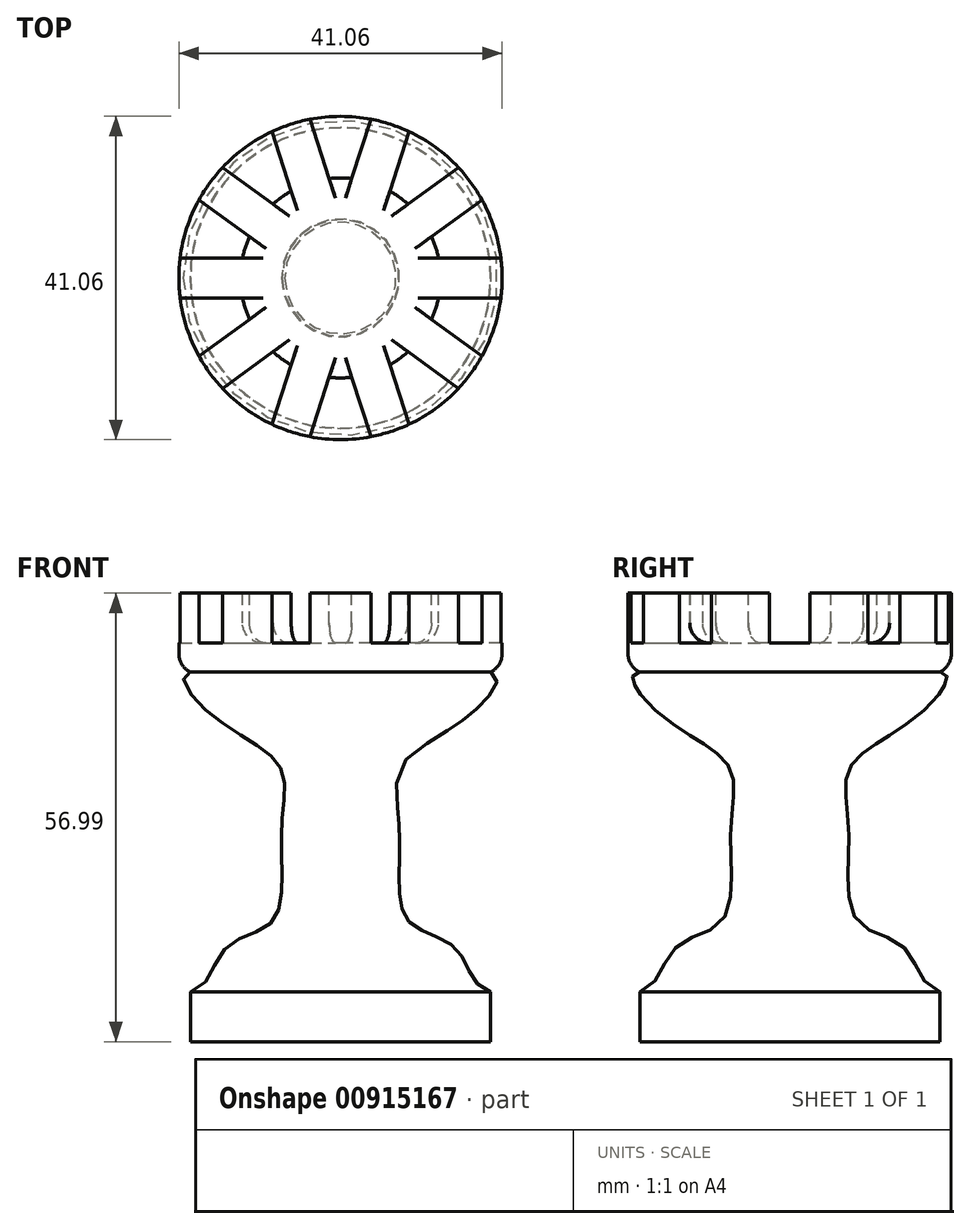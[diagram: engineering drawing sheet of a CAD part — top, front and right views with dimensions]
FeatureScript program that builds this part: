
annotation { "Feature Type Name" : "Feature", "Feature Type Description" : "" }
export const myFeature = defineFeature(function(context is Context, id is Id, definition is map)
    precondition{}
    {
        {
            var Q0;
            Q0=qCreatedBy(makeId("Front.planeOp"),FACE);
            var sketch = newSketch(context, id + "F0", { "sketchPlane" : qUnion([Q0])});
            skLineSegment(sketch, "E0", {"start": v(0, 0) * mm, "end": v(0, 57.15) * mm});
            skLineSegment(sketch, "E1", {"start": v(0, 0) * mm, "end": v(19.05, 0) * mm});
            skLineSegment(sketch, "E2", {"start": v(19.05, 0) * mm, "end": v(19.05, 6.35) * mm});
            skLineSegment(sketch, "E3", {"start": v(0, 47) * mm, "end": v(32.66, 47) * mm, "construction": true});
            skFitSpline(sketch, "E4", {"points": [v(19.05, 6.35) * mm, v(14.72, 11.76) * mm, v(8.88, 15.04) * mm, v(7.42, 20.88) * mm, v(7.42, 28.17) * mm, v(7.42, 34.37) * mm, v(11.8, 38.39) * mm, v(19.05, 44.22) * mm, v(19.11, 47) * mm], "startDerivative": vector(-57.38, 13.53) * mm, "endDerivative": vector(-50.93, 0) * mm});
            skLineSegment(sketch, "E5.bottom", {"start": v(0, 47) * mm, "end": v(20.53, 47) * mm});
            skLineSegment(sketch, "E5.top", {"start": v(0, 56.99) * mm, "end": v(20.53, 56.99) * mm});
            skLineSegment(sketch, "E5.left", {"start": v(0, 47) * mm, "end": v(0, 56.99) * mm});
            skLineSegment(sketch, "E5.right", {"start": v(20.53, 47) * mm, "end": v(20.53, 56.99) * mm});
            skSolve(sketch);
        }
        {
            var Q0;
            Q0=makeQuery(id+"F0.imprint","IMPRINT",FACE,{"disambiguationData":[TD([[makeQuery(id+"F0.imprint","IMPRINT",EDGE,{"derivedFrom":sQuery(id+"F0.wireOp",EDGE,"E5.top")}),-1.0]])]});
            var Q1;
            {var subQ1=sQuery(id+"F0.wireOp",EDGE,"E1");Q1=makeQuery(id+"F0.imprint","IMPRINT",FACE,{"disambiguationData":[TD([[makeQuery(id+"F0.imprint","IMPRINT",EDGE,{"derivedFrom":subQ1}),1.0]])]});}
            var Q2;
            Q2=sQuery(id+"F0.wireOp",EDGE,"E0");
            revolve(context, id + "F1", {"surfaceOperationType" : NewSurfaceOperationType.NEW, "entities" : qUnion([Q0, Q1]), "axis" : qUnion([Q2]), "revolveType" : RevolveType.FULL});
        }
        {
            var Q0;
            Q0=makeQuery(id+"F1.opRevolve","SWEPT_FACE",FACE,{"disambiguationData":[OSD([sQuery(id+"F0.wireOp",EDGE,"E5.top")])]});
            var sketch = newSketch(context, id + "F2", { "sketchPlane" : qUnion([Q0])});
            skCircle(sketch, "E6", {"center": v(0, 0) * mm, "radius": 12.7 * mm});
            skSolve(sketch);
        }
        {
            var Q0;
            Q0 = qSketchRegion(id + "F2", true);
            extrude(context, id + "F3", {"entities" : qUnion([Q0]), "operationType" : NewBodyOperationType.REMOVE, "oppositeDirection" : true, "depth" : 6.35 * mm, "offsetDistance" : 25.4 * mm});
        }
        {
            var Q0;
            Q0=makeQuery(id+"F1.opRevolve","SWEPT_FACE",FACE,{"disambiguationData":[OSD([sQuery(id+"F0.wireOp",EDGE,"E5.top")])]});
            var sketch = newSketch(context, id + "F4", { "sketchPlane" : qUnion([Q0])});
            skLineSegment(sketch, "E7", {"start": v(0, 0) * mm, "end": v(15.75, 0) * mm, "construction": true});
            skLineSegment(sketch, "E8.bottom", {"start": v(22.72, 2.54) * mm, "end": v(8.77, 2.54) * mm});
            skLineSegment(sketch, "E8.top", {"start": v(22.72, -2.54) * mm, "end": v(8.77, -2.54) * mm});
            skLineSegment(sketch, "E8.left", {"start": v(22.72, 2.54) * mm, "end": v(22.72, -2.54) * mm});
            skLineSegment(sketch, "E8.right", {"start": v(8.77, 2.54) * mm, "end": v(8.77, -2.54) * mm});
            skPoint(sketch, "E8.middle", {"position": v(15.75, 0) * mm});
            skLineSegment(sketch, "E9.1.0", {"start": v(19.88, 11.3) * mm, "end": v(8.59, 3.1) * mm});
            skPoint(sketch, "E9.1.1", {"position": v(12.74, 9.26) * mm});
            skLineSegment(sketch, "E9.1.2", {"start": v(5.6, 7.21) * mm, "end": v(8.59, 3.1) * mm});
            skLineSegment(sketch, "E9.1.3", {"start": v(16.9, 15.41) * mm, "end": v(5.6, 7.21) * mm});
            skLineSegment(sketch, "E9.1.4", {"start": v(16.9, 15.41) * mm, "end": v(19.88, 11.3) * mm});
            skLineSegment(sketch, "E9.2.0", {"start": v(9.44, 20.83) * mm, "end": v(5.13, 7.56) * mm});
            skPoint(sketch, "E9.2.1", {"position": v(4.87, 14.98) * mm});
            skLineSegment(sketch, "E9.2.2", {"start": v(0.3, 9.13) * mm, "end": v(5.13, 7.56) * mm});
            skLineSegment(sketch, "E9.2.3", {"start": v(4.6, 22.4) * mm, "end": v(0.3, 9.13) * mm});
            skLineSegment(sketch, "E9.2.4", {"start": v(4.6, 22.4) * mm, "end": v(9.44, 20.83) * mm});
            skLineSegment(sketch, "E9.3.0", {"start": v(-4.6, 22.4) * mm, "end": v(-0.3, 9.13) * mm});
            skPoint(sketch, "E9.3.1", {"position": v(-4.87, 14.98) * mm});
            skLineSegment(sketch, "E9.3.2", {"start": v(-5.13, 7.56) * mm, "end": v(-0.3, 9.13) * mm});
            skLineSegment(sketch, "E9.3.3", {"start": v(-9.44, 20.83) * mm, "end": v(-5.13, 7.56) * mm});
            skLineSegment(sketch, "E9.3.4", {"start": v(-9.44, 20.83) * mm, "end": v(-4.6, 22.4) * mm});
            skLineSegment(sketch, "E9.4.0", {"start": v(-16.9, 15.41) * mm, "end": v(-5.6, 7.21) * mm});
            skPoint(sketch, "E9.4.1", {"position": v(-12.74, 9.26) * mm});
            skLineSegment(sketch, "E9.4.2", {"start": v(-8.59, 3.1) * mm, "end": v(-5.6, 7.21) * mm});
            skLineSegment(sketch, "E9.4.3", {"start": v(-19.88, 11.3) * mm, "end": v(-8.59, 3.1) * mm});
            skLineSegment(sketch, "E9.4.4", {"start": v(-19.88, 11.3) * mm, "end": v(-16.9, 15.41) * mm});
            skLineSegment(sketch, "E9.5.0", {"start": v(-22.72, 2.54) * mm, "end": v(-8.77, 2.54) * mm});
            skPoint(sketch, "E9.5.1", {"position": v(-15.75, 0) * mm});
            skLineSegment(sketch, "E9.5.2", {"start": v(-8.77, -2.54) * mm, "end": v(-8.77, 2.54) * mm});
            skLineSegment(sketch, "E9.5.3", {"start": v(-22.72, -2.54) * mm, "end": v(-8.77, -2.54) * mm});
            skLineSegment(sketch, "E9.5.4", {"start": v(-22.72, -2.54) * mm, "end": v(-22.72, 2.54) * mm});
            skLineSegment(sketch, "E9.6.0", {"start": v(-19.88, -11.3) * mm, "end": v(-8.59, -3.1) * mm});
            skPoint(sketch, "E9.6.1", {"position": v(-12.74, -9.26) * mm});
            skLineSegment(sketch, "E9.6.2", {"start": v(-5.6, -7.21) * mm, "end": v(-8.59, -3.1) * mm});
            skLineSegment(sketch, "E9.6.3", {"start": v(-16.9, -15.41) * mm, "end": v(-5.6, -7.21) * mm});
            skLineSegment(sketch, "E9.6.4", {"start": v(-16.9, -15.41) * mm, "end": v(-19.88, -11.3) * mm});
            skLineSegment(sketch, "E9.7.0", {"start": v(-9.44, -20.83) * mm, "end": v(-5.13, -7.56) * mm});
            skPoint(sketch, "E9.7.1", {"position": v(-4.87, -14.98) * mm});
            skLineSegment(sketch, "E9.7.2", {"start": v(-0.3, -9.13) * mm, "end": v(-5.13, -7.56) * mm});
            skLineSegment(sketch, "E9.7.3", {"start": v(-4.6, -22.4) * mm, "end": v(-0.3, -9.13) * mm});
            skLineSegment(sketch, "E9.7.4", {"start": v(-4.6, -22.4) * mm, "end": v(-9.44, -20.83) * mm});
            skLineSegment(sketch, "E9.8.0", {"start": v(4.6, -22.4) * mm, "end": v(0.3, -9.13) * mm});
            skPoint(sketch, "E9.8.1", {"position": v(4.87, -14.98) * mm});
            skLineSegment(sketch, "E9.8.2", {"start": v(5.13, -7.56) * mm, "end": v(0.3, -9.13) * mm});
            skLineSegment(sketch, "E9.8.3", {"start": v(9.44, -20.83) * mm, "end": v(5.13, -7.56) * mm});
            skLineSegment(sketch, "E9.8.4", {"start": v(9.44, -20.83) * mm, "end": v(4.6, -22.4) * mm});
            skLineSegment(sketch, "E9.9.0", {"start": v(16.9, -15.41) * mm, "end": v(5.6, -7.21) * mm});
            skPoint(sketch, "E9.9.1", {"position": v(12.74, -9.26) * mm});
            skLineSegment(sketch, "E9.9.2", {"start": v(8.59, -3.1) * mm, "end": v(5.6, -7.21) * mm});
            skLineSegment(sketch, "E9.9.3", {"start": v(19.88, -11.3) * mm, "end": v(8.59, -3.1) * mm});
            skLineSegment(sketch, "E9.9.4", {"start": v(19.88, -11.3) * mm, "end": v(16.9, -15.41) * mm});
            skPoint(sketch, "E9.center", {"position": v(0, 0) * mm});
            skSolve(sketch);
        }
        {
            var Q0;
            Q0 = qSketchRegion(id + "F4", true);
            extrude(context, id + "F5", {"entities" : qUnion([Q0]), "operationType" : NewBodyOperationType.REMOVE, "oppositeDirection" : true, "depth" : 6.35 * mm, "offsetDistance" : 25.4 * mm});
        }
        {
            var Q0;
            Q0=makeQuery(id+"F1.opRevolve","SWEPT_EDGE",EDGE,{"disambiguationData":[OSD([sQuery(id+"F0.wireOp",EDGE,"E5.bottom"),sQuery(id+"F0.wireOp",EDGE,"E5.right")])]});
            var Q1;
            {var subQ0=sQuery(id+"F4.wireOp",EDGE,"E9.6.3");var subQ1=sQuery(id+"F2.wireOp",EDGE,"E6");Q1=makeQuery(id+"F5.boolean.opBoolean","SPLIT",EDGE,{"disambiguationData":[TD([makeQuery(id+"F5.opExtrude","SWEPT_FACE",FACE,{"disambiguationData":[OSD([subQ0])]})])],"derivedFrom":makeQuery(id+"F3.boolean.opBoolean","COPY",EDGE,{"derivedFrom":makeQuery(id+"F3.opExtrude","CAP_EDGE",EDGE,{"disambiguationData":[OSD([subQ1])],"isStart":false})})});}
            var Q2;
            {var subQ0=sQuery(id+"F4.wireOp",EDGE,"E9.5.3");var subQ1=sQuery(id+"F2.wireOp",EDGE,"E6");Q2=makeQuery(id+"F5.boolean.opBoolean","SPLIT",EDGE,{"disambiguationData":[TD([makeQuery(id+"F5.opExtrude","SWEPT_FACE",FACE,{"disambiguationData":[OSD([subQ0])]})])],"derivedFrom":makeQuery(id+"F3.boolean.opBoolean","COPY",EDGE,{"derivedFrom":makeQuery(id+"F3.opExtrude","CAP_EDGE",EDGE,{"disambiguationData":[OSD([subQ1])],"isStart":false})})});}
            var Q3;
            {var subQ0=sQuery(id+"F4.wireOp",EDGE,"E9.4.3");var subQ1=sQuery(id+"F2.wireOp",EDGE,"E6");Q3=makeQuery(id+"F5.boolean.opBoolean","SPLIT",EDGE,{"disambiguationData":[TD([makeQuery(id+"F5.opExtrude","SWEPT_FACE",FACE,{"disambiguationData":[OSD([subQ0])]})])],"derivedFrom":makeQuery(id+"F3.boolean.opBoolean","COPY",EDGE,{"derivedFrom":makeQuery(id+"F3.opExtrude","CAP_EDGE",EDGE,{"disambiguationData":[OSD([subQ1])],"isStart":false})})});}
            var Q4;
            {var subQ0=sQuery(id+"F2.wireOp",EDGE,"E6");var subQ2=sQuery(id+"F4.wireOp",EDGE,"E9.7.3");Q4=makeQuery(id+"F5.boolean.opBoolean","SPLIT",EDGE,{"disambiguationData":[TD([makeQuery(id+"F5.opExtrude","SWEPT_FACE",FACE,{"disambiguationData":[OSD([subQ2])]})])],"derivedFrom":makeQuery(id+"F3.boolean.opBoolean","COPY",EDGE,{"derivedFrom":makeQuery(id+"F3.opExtrude","CAP_EDGE",EDGE,{"disambiguationData":[OSD([subQ0])],"isStart":false})})});}
            var Q5;
            {var subQ0=sQuery(id+"F2.wireOp",EDGE,"E6");var subQ2=sQuery(id+"F4.wireOp",EDGE,"E9.8.3");Q5=makeQuery(id+"F5.boolean.opBoolean","SPLIT",EDGE,{"disambiguationData":[TD([makeQuery(id+"F5.opExtrude","SWEPT_FACE",FACE,{"disambiguationData":[OSD([subQ2])]})])],"derivedFrom":makeQuery(id+"F3.boolean.opBoolean","COPY",EDGE,{"derivedFrom":makeQuery(id+"F3.opExtrude","CAP_EDGE",EDGE,{"disambiguationData":[OSD([subQ0])],"isStart":false})})});}
            var Q6;
            {var subQ0=sQuery(id+"F4.wireOp",EDGE,"E8.top");var subQ1=sQuery(id+"F2.wireOp",EDGE,"E6");Q6=makeQuery(id+"F5.boolean.opBoolean","SPLIT",EDGE,{"disambiguationData":[TD([makeQuery(id+"F5.opExtrude","SWEPT_FACE",FACE,{"disambiguationData":[OSD([subQ0])]})])],"derivedFrom":makeQuery(id+"F3.boolean.opBoolean","COPY",EDGE,{"derivedFrom":makeQuery(id+"F3.opExtrude","CAP_EDGE",EDGE,{"disambiguationData":[OSD([subQ1])],"isStart":false})})});}
            var Q7;
            {var subQ0=sQuery(id+"F2.wireOp",EDGE,"E6");var subQ2=sQuery(id+"F4.wireOp",EDGE,"E8.bottom");Q7=makeQuery(id+"F5.boolean.opBoolean","SPLIT",EDGE,{"disambiguationData":[TD([makeQuery(id+"F5.opExtrude","SWEPT_FACE",FACE,{"disambiguationData":[OSD([subQ2])]})])],"derivedFrom":makeQuery(id+"F3.boolean.opBoolean","COPY",EDGE,{"derivedFrom":makeQuery(id+"F3.opExtrude","CAP_EDGE",EDGE,{"disambiguationData":[OSD([subQ0])],"isStart":false})})});}
            var Q8;
            {var subQ0=sQuery(id+"F2.wireOp",EDGE,"E6");var subQ2=sQuery(id+"F4.wireOp",EDGE,"E9.1.3");Q8=makeQuery(id+"F5.boolean.opBoolean","SPLIT",EDGE,{"disambiguationData":[TD([makeQuery(id+"F5.opExtrude","SWEPT_FACE",FACE,{"disambiguationData":[OSD([subQ2])]})])],"derivedFrom":makeQuery(id+"F3.boolean.opBoolean","COPY",EDGE,{"derivedFrom":makeQuery(id+"F3.opExtrude","CAP_EDGE",EDGE,{"disambiguationData":[OSD([subQ0])],"isStart":false})})});}
            var Q9;
            {var subQ1=sQuery(id+"F4.wireOp",EDGE,"E9.3.3");var subQ2=sQuery(id+"F2.wireOp",EDGE,"E6");Q9=makeQuery(id+"F5.boolean.opBoolean","SPLIT",EDGE,{"disambiguationData":[TD([makeQuery(id+"F5.opExtrude","SWEPT_FACE",FACE,{"disambiguationData":[OSD([subQ1])]})])],"derivedFrom":makeQuery(id+"F3.boolean.opBoolean","COPY",EDGE,{"derivedFrom":makeQuery(id+"F3.opExtrude","CAP_EDGE",EDGE,{"disambiguationData":[OSD([subQ2])],"isStart":false})})});}
            var Q10;
            {var subQ1=sQuery(id+"F2.wireOp",EDGE,"E6");var subQ2=sQuery(id+"F4.wireOp",EDGE,"E9.2.3");Q10=makeQuery(id+"F5.boolean.opBoolean","SPLIT",EDGE,{"disambiguationData":[TD([makeQuery(id+"F5.opExtrude","SWEPT_FACE",FACE,{"disambiguationData":[OSD([subQ2])]})])],"derivedFrom":makeQuery(id+"F3.boolean.opBoolean","COPY",EDGE,{"derivedFrom":makeQuery(id+"F3.opExtrude","CAP_EDGE",EDGE,{"disambiguationData":[OSD([subQ1])],"isStart":false})})});}
            fillet(context, id + "F6", {"entities" : qUnion([Q0, Q1, Q2, Q3, Q4, Q5, Q6, Q7, Q8, Q9, Q10]), "radius" : 2.54 * mm, "tangentPropagation" : true, "allowEdgeOverflow" : false});
        }
    });
